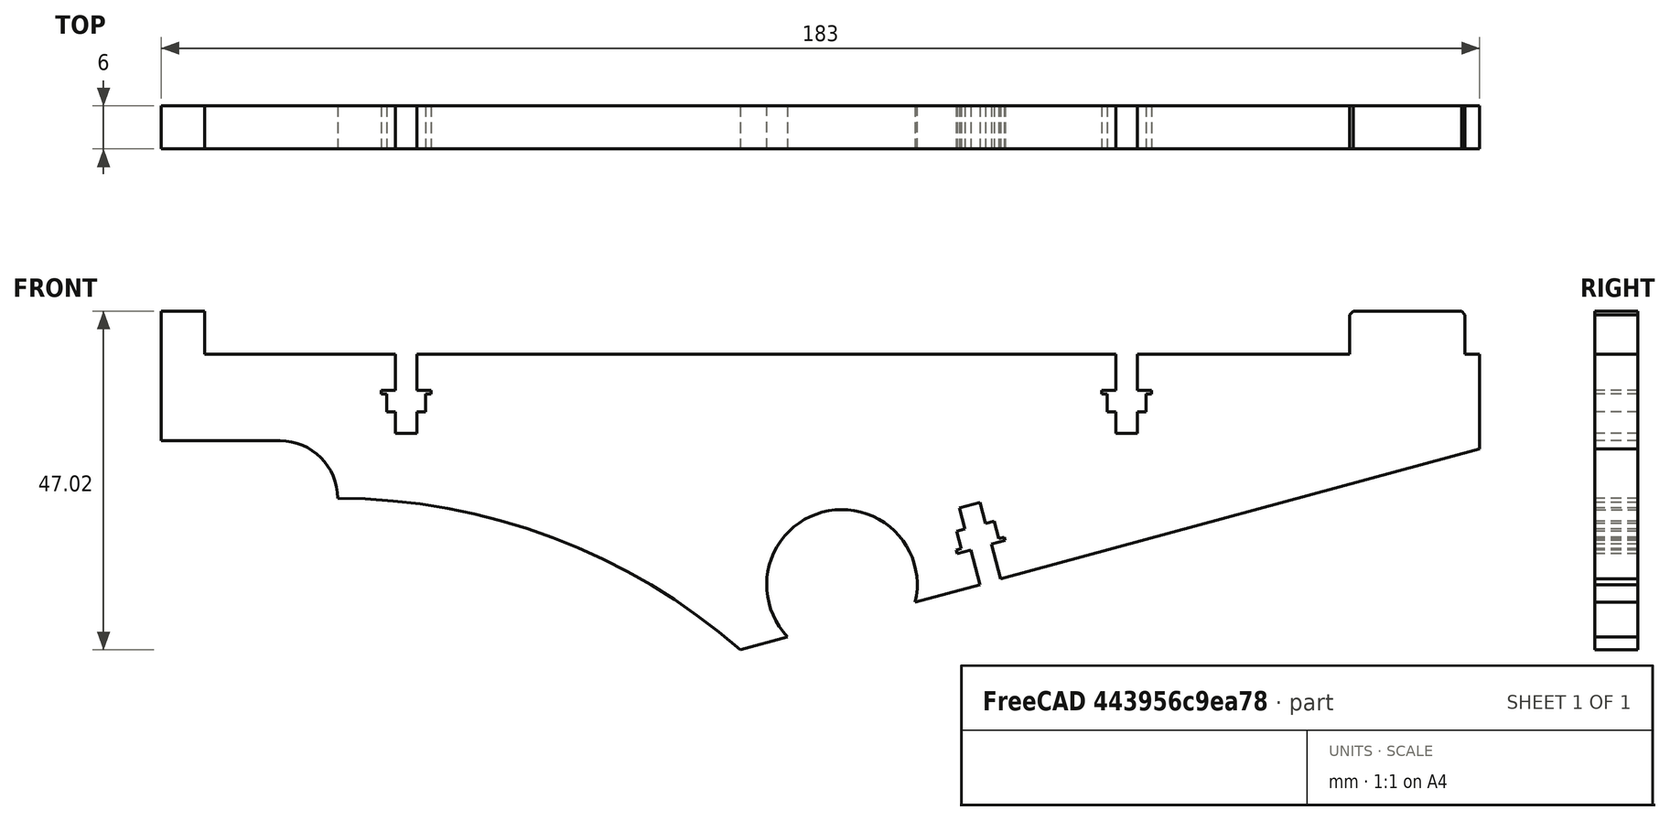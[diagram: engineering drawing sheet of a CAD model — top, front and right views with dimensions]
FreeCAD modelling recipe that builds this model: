
FCSTD DOCUMENT  (FreeCAD 0.17R13541 (Git))
Label: xx_xxx_y-cross-rib
License: All rights reserved
LicenseURL: http://en.wikipedia.org/wiki/All_rights_reserved
objects: Sketcher::SketchObject×1, PartDesign::Pad×1, PartDesign::Body×1
note: 4 computed .brp shape members not serialized (recipe doc carries the construction recipe); baked Part::Feature solids carry a one-line shape summary decoded from their .brp

FEATURE [Sketcher::SketchObject] Sketch065
  MapMode = 5
  Placement = pos=(0,0,0) rot=(1,0,0;1.5708rad)
  Support = -> [XZ_Plane]
  sketch-geometry (65):
    g0: LineSegment StartX=98.7285 StartY=-6.36814 StartZ=0 EndX=100.63 EndY=-5.85162 EndZ=0
    g1: LineSegment StartX=118.98 StartY=9 StartZ=0 EndX=116.02 EndY=9 EndZ=0
    g2: LineSegment StartX=20.2 StartY=14.5 StartZ=0 EndX=20.2 EndY=12 EndZ=0
    g3: LineSegment StartX=114.05 StartY=14.5 StartZ=0 EndX=114.05 EndY=15 EndZ=0
    g4: LineSegment StartX=93.8399 StartY=-7.17823 StartZ=0 EndX=93.971 EndY=-7.66074 EndZ=0
    g5: LineSegment StartX=120.95 StartY=15 StartZ=0 EndX=120.95 EndY=14.5 EndZ=0
    g6: LineSegment StartX=88.1661 StartY=-14.4192 StartZ=0 EndX=97.1831 EndY=-11.9693 EndZ=0
    g7: LineSegment StartX=100.039 StartY=-11.1932 StartZ=0 EndX=166.5 EndY=6.86384 EndZ=0
    g8: LineSegment StartX=95.8721 StartY=-7.14422 StartZ=0 EndX=97.1831 EndY=-11.9693 EndZ=0
    g9: LineSegment StartX=16.02 StartY=12 StartZ=0 EndX=14.8 EndY=12 EndZ=0
    g10: LineSegment StartX=118.98 StartY=20 StartZ=0 EndX=118.98 EndY=15 EndZ=0
    g11: LineSegment StartX=63.8707 StartY=-21.0201 StartZ=0 EndX=70.4558 EndY=-19.231 EndZ=0
    g12: LineSegment StartX=93.971 StartY=-7.66074 StartZ=0 EndX=95.8721 EndY=-7.14422 EndZ=0
    g13: LineSegment StartX=14.8 StartY=12 StartZ=0 EndX=14.8 EndY=14.5 EndZ=0
    g14: LineSegment StartX=148.5 StartY=20 StartZ=0 EndX=118.98 EndY=20 EndZ=0
    g15: LineSegment StartX=-10.5 StartY=20 StartZ=0 EndX=-10.5 EndY=26 EndZ=0
    g16: LineSegment StartX=93.9082 StartY=-4.56905 StartZ=0 EndX=94.5637 EndY=-6.98159 EndZ=0
    g17: ArcOfCircle CenterX=0 CenterY=0 CenterZ=0 NormalX=0 NormalY=0 NormalZ=1 AngleXU=0 Radius=8 StartAngle=0 EndAngle=1.5708
    g18: LineSegment StartX=94.2989 StartY=-1.35413 StartZ=0 EndX=95.0855 EndY=-4.24917 EndZ=0
    g19: LineSegment StartX=14.05 StartY=15 StartZ=0 EndX=16.02 EndY=15 EndZ=0
    g20: LineSegment StartX=97.1554 StartY=-0.57804 StartZ=0 EndX=94.2989 EndY=-1.35413 EndZ=0
    g21: LineSegment StartX=166.5 StartY=6.86384 StartZ=0 EndX=166.5 EndY=20 EndZ=0
    g22: LineSegment StartX=97.942 StartY=-3.47309 StartZ=0 EndX=97.1554 EndY=-0.57804 EndZ=0
    g23: LineSegment StartX=99.7748 StartY=-5.56576 StartZ=0 EndX=99.1193 EndY=-3.15322 EndZ=0
    g24: LineSegment StartX=94.5637 StartY=-6.98159 StartZ=0 EndX=93.8399 EndY=-7.17823 EndZ=0
    g25: LineSegment StartX=99.1193 StartY=-3.15322 StartZ=0 EndX=97.942 EndY=-3.47309 EndZ=0
    g26: LineSegment StartX=118.98 StartY=12 StartZ=0 EndX=118.98 EndY=9 EndZ=0
    g27: LineSegment StartX=120.95 StartY=14.5 StartZ=0 EndX=120.2 EndY=14.5 EndZ=0
    g28: LineSegment StartX=18.98 StartY=12 StartZ=0 EndX=18.98 EndY=9 EndZ=0
    g29: LineSegment StartX=16.02 StartY=15 StartZ=0 EndX=16.02 EndY=20 EndZ=0
    g30: LineSegment StartX=116.02 StartY=15 StartZ=0 EndX=116.02 EndY=20 EndZ=0
    g31: LineSegment StartX=164.5 StartY=25.5 StartZ=0 EndX=164 EndY=26 EndZ=0
    g32: ArcOfCircle CenterX=78 CenterY=-12 CenterZ=0 NormalX=0 NormalY=0 NormalZ=1 AngleXU=0 Radius=10.45 StartAngle=6.04957 EndAngle=10.189
    g33: LineSegment StartX=18.98 StartY=9 StartZ=0 EndX=16.02 EndY=9 EndZ=0
    g34: LineSegment StartX=100.039 StartY=-11.1932 StartZ=0 EndX=98.7285 EndY=-6.36814 EndZ=0
    g35: LineSegment StartX=116.02 StartY=9 StartZ=0 EndX=116.02 EndY=12 EndZ=0
    g36: LineSegment StartX=100.63 StartY=-5.85162 StartZ=0 EndX=100.499 EndY=-5.36911 EndZ=0
    g37: LineSegment StartX=14.05 StartY=14.5 StartZ=0 EndX=14.05 EndY=15 EndZ=0
    g38: LineSegment StartX=116.02 StartY=12 StartZ=0 EndX=114.8 EndY=12 EndZ=0
    g39: LineSegment StartX=164 StartY=26 StartZ=0 EndX=149 EndY=26 EndZ=0
    g40: LineSegment StartX=116.02 StartY=20 StartZ=0 EndX=18.98 EndY=20 EndZ=0
    g41: LineSegment StartX=114.8 StartY=14.5 StartZ=0 EndX=114.05 EndY=14.5 EndZ=0
    g42: LineSegment StartX=164.5 StartY=20 StartZ=0 EndX=164.5 EndY=25.5 EndZ=0
    g43: LineSegment StartX=148.5 StartY=25.5 StartZ=0 EndX=148.5 EndY=20 EndZ=0
    g44: LineSegment StartX=16.02 StartY=20 StartZ=0 EndX=-10.5 EndY=20 EndZ=0
    g45: LineSegment StartX=-16.5 StartY=26 StartZ=0 EndX=-16.5 EndY=8 EndZ=0
    g46: LineSegment StartX=20.95 StartY=15 StartZ=0 EndX=20.95 EndY=14.5 EndZ=0
    g47: LineSegment StartX=95.0855 StartY=-4.24917 StartZ=0 EndX=93.9082 EndY=-4.56905 EndZ=0
    g48: LineSegment StartX=14.8 StartY=14.5 StartZ=0 EndX=14.05 EndY=14.5 EndZ=0
    g49: LineSegment StartX=118.98 StartY=15 StartZ=0 EndX=120.95 EndY=15 EndZ=0
    g50: LineSegment StartX=120.2 StartY=12 StartZ=0 EndX=118.98 EndY=12 EndZ=0
    g51: LineSegment StartX=149 StartY=26 StartZ=0 EndX=148.5 EndY=25.5 EndZ=0
    g52: LineSegment StartX=114.05 StartY=15 StartZ=0 EndX=116.02 EndY=15 EndZ=0
    g53: LineSegment StartX=20.2 StartY=12 StartZ=0 EndX=18.98 EndY=12 EndZ=0
    g54: LineSegment StartX=114.8 StartY=12 StartZ=0 EndX=114.8 EndY=14.5 EndZ=0
    g55: LineSegment StartX=166.5 StartY=20 StartZ=0 EndX=164.5 EndY=20 EndZ=0
    g56: LineSegment StartX=18.98 StartY=20 StartZ=0 EndX=18.98 EndY=15 EndZ=0
    g57: LineSegment StartX=-10.5 StartY=26 StartZ=0 EndX=-16.5 EndY=26 EndZ=0
    g58: LineSegment StartX=18.98 StartY=15 StartZ=0 EndX=20.95 EndY=15 EndZ=0
    g59: LineSegment StartX=100.499 StartY=-5.36911 StartZ=0 EndX=99.7748 EndY=-5.56576 EndZ=0
    g60: ArcOfCircle CenterX=8 CenterY=-84.7611 CenterZ=0 NormalX=0 NormalY=0 NormalZ=1 AngleXU=0 Radius=84.7611 StartAngle=0.851102 EndAngle=1.5708
    g61: LineSegment StartX=-16.5 StartY=8 StartZ=0 EndX=-6.58548e-07 EndY=8 EndZ=0
    g62: LineSegment StartX=120.2 StartY=14.5 StartZ=0 EndX=120.2 EndY=12 EndZ=0
    g63: LineSegment StartX=20.95 StartY=14.5 StartZ=0 EndX=20.2 EndY=14.5 EndZ=0
    g64: LineSegment StartX=16.02 StartY=9 StartZ=0 EndX=16.02 EndY=12 EndZ=0
  constraints (65):
    c: Coincident(g45,g61)
    c: Coincident(g45,g57)
    c: Coincident(g15,g44)
    c: Coincident(g57,g15)
    c: Coincident(g17,g61)
    c: Coincident(g60,g17)
    c: Coincident(g48,g37)
    c: Coincident(g37,g19)
    c: Coincident(g13,g9)
    c: Coincident(g48,g13)
    c: Coincident(g64,g33)
    c: Coincident(g64,g9)
    c: Coincident(g19,g29)
    c: Coincident(g29,g44)
    c: Coincident(g28,g33)
    c: Coincident(g28,g53)
    c: Coincident(g58,g56)
    c: Coincident(g56,g40)
    c: Coincident(g53,g2)
    c: Coincident(g2,g63)
    c: Coincident(g63,g46)
    c: Coincident(g58,g46)
    c: Coincident(g11,g60)
    c: Coincident(g32,g11)
    c: Coincident(g6,g32)
    c: Coincident(g4,g24)
    c: Coincident(g47,g16)
    c: Coincident(g4,g12)
    c: Coincident(g18,g20)
    c: Coincident(g24,g16)
    c: Coincident(g47,g18)
    c: Coincident(g12,g8)
    c: Coincident(g22,g20)
    c: Coincident(g8,g6)
    c: Coincident(g25,g22)
    c: Coincident(g34,g0)
    c: Coincident(g25,g23)
    c: Coincident(g23,g59)
    c: Coincident(g34,g7)
    c: Coincident(g59,g36)
    c: Coincident(g36,g0)
    c: Coincident(g3,g41)
    c: Coincident(g52,g3)
    c: Coincident(g38,g54)
    c: Coincident(g41,g54)
    c: Coincident(g35,g1)
    c: Coincident(g38,g35)
    c: Coincident(g30,g52)
    c: Coincident(g30,g40)
    c: Coincident(g1,g26)
    c: Coincident(g50,g26)
    c: Coincident(g49,g10)
    c: Coincident(g10,g14)
    c: Coincident(g62,g50)
    c: Coincident(g62,g27)
    c: Coincident(g27,g5)
    c: Coincident(g5,g49)
    c: Coincident(g14,g43)
    c: Coincident(g51,g43)
    c: Coincident(g51,g39)
    c: Coincident(g31,g39)
    c: Coincident(g55,g42)
    c: Coincident(g31,g42)
    c: Coincident(g21,g7)
    c: Coincident(g21,g55)
FEATURE [PartDesign::Pad] Pad
  Length = 6
  Length2 = 100
  Placement = pos=(0,0,0) rot=(1,0,0;1.5708rad)
  Profile = -> Sketch065
  Type = 0
FEATURE [PartDesign::Body] Body
  Group = -> [Sketch065,Pad]
  Origin = -> Origin
  Tip = -> Pad
